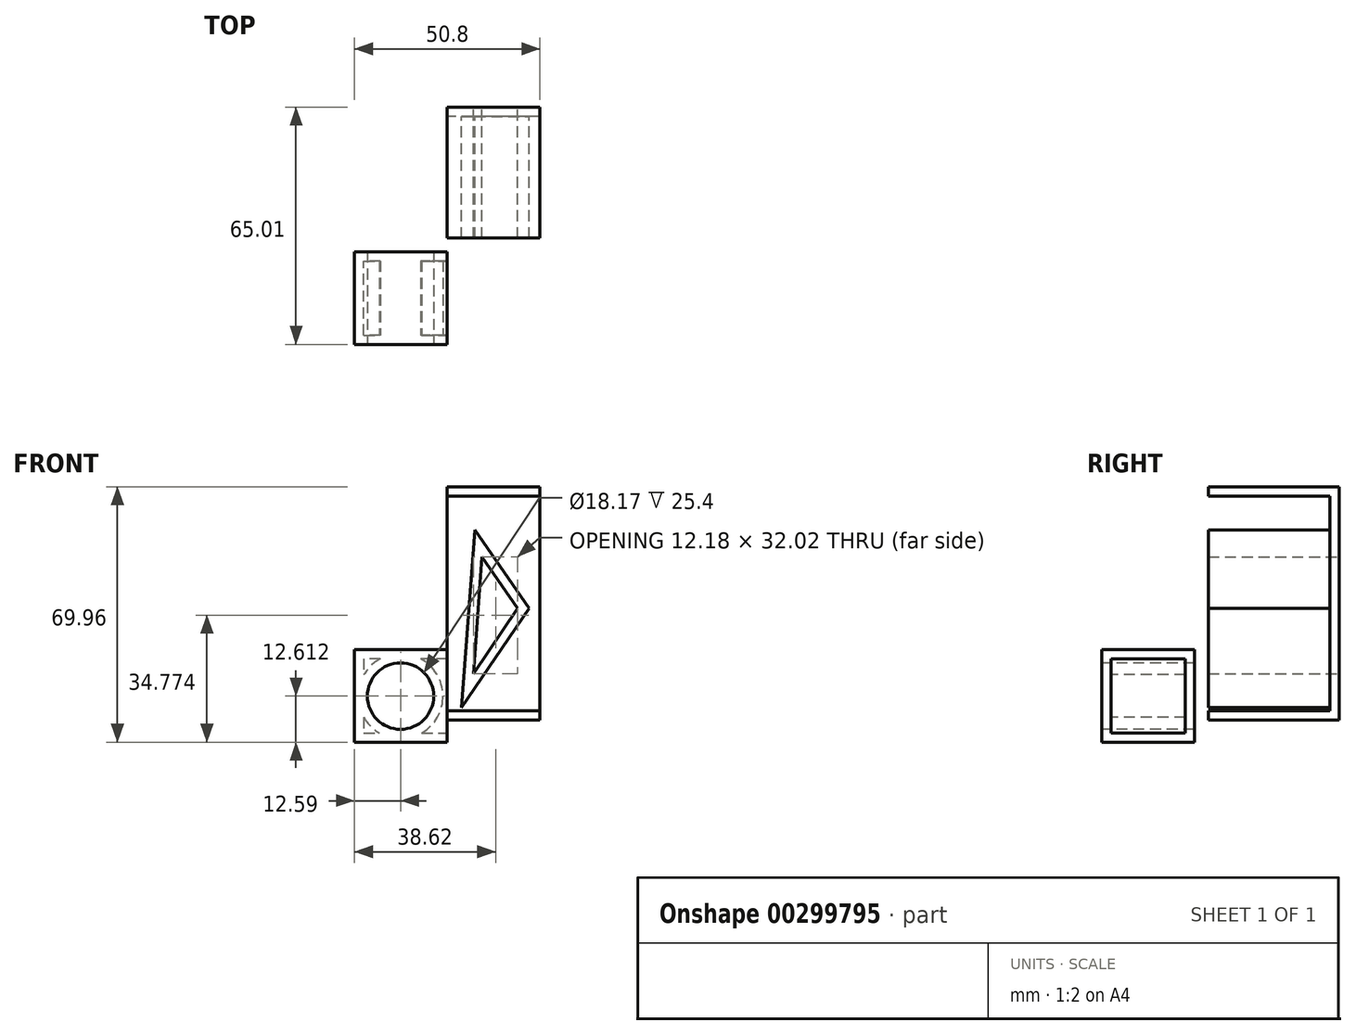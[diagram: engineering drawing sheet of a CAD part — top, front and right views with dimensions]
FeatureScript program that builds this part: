
annotation { "Feature Type Name" : "Feature", "Feature Type Description" : "" }
export const myFeature = defineFeature(function(context is Context, id is Id, definition is map)
    precondition{}
    {
        {
            var Q0;
            Q0=qCreatedBy(makeId("Front.planeOp"),FACE);
            var sketch = newSketch(context, id + "F0", { "sketchPlane" : qUnion([Q0])});
            skLineSegment(sketch, "E0", {"start": v(0, 25.4) * mm, "end": v(-25.4, 25.4) * mm});
            skLineSegment(sketch, "E1", {"start": v(-25.4, 25.4) * mm, "end": v(-25.4, 0) * mm});
            skLineSegment(sketch, "E2", {"start": v(-25.4, 0) * mm, "end": v(0, 0) * mm});
            skLineSegment(sketch, "E3", {"start": v(0, 0) * mm, "end": v(0, 25.4) * mm});
            skSolve(sketch);
        }
        {
            var Q0;
            Q0=makeQuery(id+"F0.imprint","IMPRINT",FACE,{"disambiguationData":[TD([[makeQuery(id+"F0.imprint","IMPRINT",EDGE,{"derivedFrom":sQuery(id+"F0.wireOp",EDGE,"E0")}),1.0]])]});
            extrude(context, id + "F1", {"entities" : qUnion([Q0]), "depth" : 25.4 * mm});
        }
        {
            var Q0;
            Q0=makeQuery(id+"F1.opExtrude","CAP_FACE",FACE,{"disambiguationData":[OSD([sQuery(id+"F0.wireOp",EDGE,"E0"),sQuery(id+"F0.wireOp",EDGE,"E1"),sQuery(id+"F0.wireOp",EDGE,"E2"),sQuery(id+"F0.wireOp",EDGE,"E3")])],"isStart":false});
            var sketch = newSketch(context, id + "F2", { "sketchPlane" : qUnion([Q0])});
            skCircle(sketch, "E4", {"center": v(-12.8, 12.61) * mm, "radius": 9.08 * mm});
            skSolve(sketch);
        }
        {
            var Q0;
            Q0 = qSketchRegion(id + "F2", true);
            extrude(context, id + "F3", {"entities" : qUnion([Q0]), "operationType" : NewBodyOperationType.REMOVE, "oppositeDirection" : true, "depth" : 25.4 * mm});
        }
        {
            var Q0;
            Q0=qCreatedBy(makeId("Right.planeOp"),FACE);
            var sketch = newSketch(context, id + "F4", { "sketchPlane" : qUnion([Q0])});
            skLineSegment(sketch, "E5.bottom", {"start": v(39.61, 6.1) * mm, "end": v(3.74, 6.1) * mm});
            skLineSegment(sketch, "E5.top", {"start": v(39.61, 69.96) * mm, "end": v(3.74, 69.96) * mm});
            skLineSegment(sketch, "E5.left", {"start": v(39.61, 6.1) * mm, "end": v(39.61, 69.96) * mm});
            skLineSegment(sketch, "E5.right", {"start": v(3.74, 6.1) * mm, "end": v(3.74, 69.96) * mm});
            skPoint(sketch, "E5.middle", {"position": v(21.68, 38.03) * mm});
            skSolve(sketch);
        }
        {
            var Q0;
            Q0 = qSketchRegion(id + "F4", true);
            extrude(context, id + "F5", {"entities" : qUnion([Q0]), "depth" : 25.4 * mm});
        }
        {
            var Q0;
            Q0=makeQuery(id+"F5.opExtrude","SWEPT_FACE",FACE,{"disambiguationData":[OSD([sQuery(id+"F4.wireOp",EDGE,"E5.left")])]});
            var sketch = newSketch(context, id + "F6", { "sketchPlane" : qUnion([Q0])});
            skLineSegment(sketch, "E6", {"start": v(-9.52, 50.78) * mm, "end": v(-19.3, 36.61) * mm});
            skLineSegment(sketch, "E7", {"start": v(-19.3, 36.61) * mm, "end": v(-7.13, 18.76) * mm});
            skLineSegment(sketch, "E8", {"start": v(-7.13, 18.76) * mm, "end": v(-9.52, 50.78) * mm});
            skSolve(sketch);
        }
        {
            var Q0;
            Q0 = qSketchRegion(id + "F6", true);
            extrude(context, id + "F7", {"entities" : qUnion([Q0]), "operationType" : NewBodyOperationType.REMOVE, "oppositeDirection" : true, "depth" : 70.61 * mm});
        }
        {
            var Q0;
            Q0=makeQuery(id+"F1.opExtrude","SWEPT_FACE",FACE,{"disambiguationData":[OSD([sQuery(id+"F0.wireOp",EDGE,"E3")])]});
            var Q1;
            Q1=makeQuery(id+"F5.opExtrude","SWEPT_FACE",FACE,{"disambiguationData":[OSD([sQuery(id+"F4.wireOp",EDGE,"E5.right")])]});
            var Q2;
            Q2=makeQuery(id+"F5.opExtrude","CAP_FACE",FACE,{"disambiguationData":[OSD([sQuery(id+"F4.wireOp",EDGE,"E5.bottom"),sQuery(id+"F4.wireOp",EDGE,"E5.top"),sQuery(id+"F4.wireOp",EDGE,"E5.left"),sQuery(id+"F4.wireOp",EDGE,"E5.right")])],"isStart":false});
            var Q3;
            Q3=makeQuery(id+"F5.opExtrude","CAP_FACE",FACE,{"disambiguationData":[OSD([sQuery(id+"F4.wireOp",EDGE,"E5.bottom"),sQuery(id+"F4.wireOp",EDGE,"E5.top"),sQuery(id+"F4.wireOp",EDGE,"E5.left"),sQuery(id+"F4.wireOp",EDGE,"E5.right")])],"isStart":true});
            shell(context, id + "F8", {"entities" : qUnion([Q0, Q1, Q2, Q3]), "thickness" : 2.54 * mm});
        }
    });
